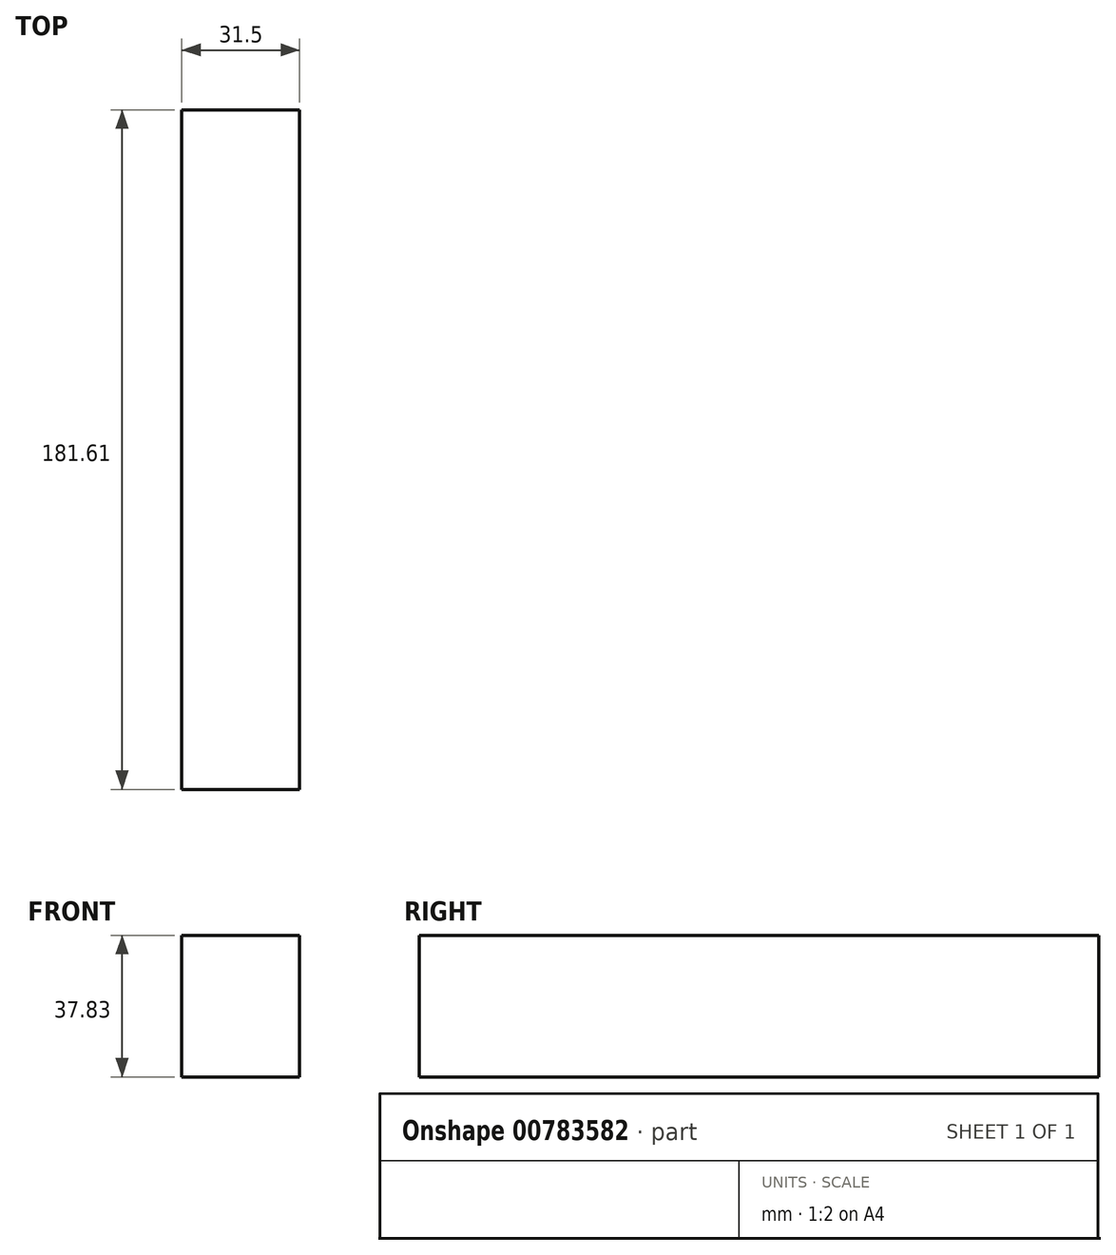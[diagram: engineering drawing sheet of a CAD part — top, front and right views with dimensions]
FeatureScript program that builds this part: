
annotation { "Feature Type Name" : "Feature", "Feature Type Description" : "" }
export const myFeature = defineFeature(function(context is Context, id is Id, definition is map)
    precondition{}
    {
        {
            var Q0;
            Q0=qCreatedBy(makeId("Front.planeOp"),FACE);
            var sketch = newSketch(context, id + "F0", { "sketchPlane" : qUnion([Q0])});
            skLineSegment(sketch, "E0.bottom", {"start": v(-55.8, 66.84) * mm, "end": v(-24.3, 66.84) * mm});
            skLineSegment(sketch, "E0.top", {"start": v(-55.8, 29.01) * mm, "end": v(-24.3, 29.01) * mm});
            skLineSegment(sketch, "E0.left", {"start": v(-55.8, 66.84) * mm, "end": v(-55.8, 29.01) * mm});
            skLineSegment(sketch, "E0.right", {"start": v(-24.3, 66.84) * mm, "end": v(-24.3, 29.01) * mm});
            skSolve(sketch);
        }
        {
            var Q0;
            Q0 = qSketchRegion(id + "F0", true);
            extrude(context, id + "F1", {"entities" : qUnion([Q0]), "depth" : 181.6 * mm, "offsetDistance" : 25.4 * mm});
        }
    });
